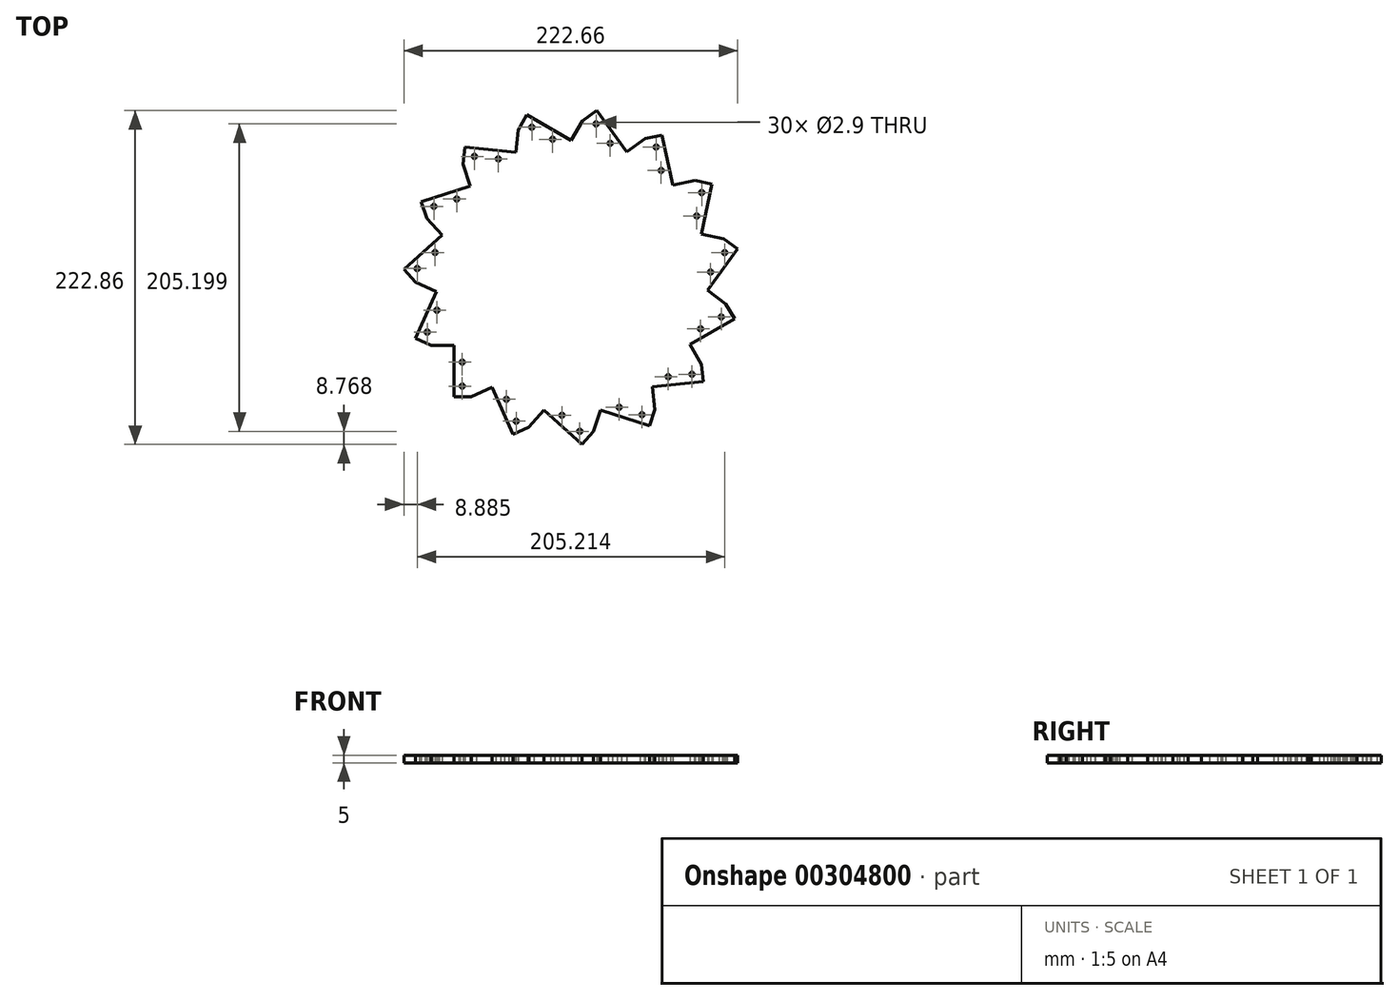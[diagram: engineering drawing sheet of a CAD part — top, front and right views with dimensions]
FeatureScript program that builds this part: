
annotation { "Feature Type Name" : "Feature", "Feature Type Description" : "" }
export const myFeature = defineFeature(function(context is Context, id is Id, definition is map)
    precondition{}
    {
        {
            var Q0;
            Q0=qCreatedBy(makeId("Top.planeOp"),FACE);
            var sketch = newSketch(context, id + "F0", { "sketchPlane" : qUnion([Q0])});
            skCircle(sketch, "E0.1.0", {"center": v(-64.96, 80.33) * mm, "radius": 1.45 * mm});
            skCircle(sketch, "E0.1.1", {"center": v(-49.05, 78.66) * mm, "radius": 1.45 * mm});
            skCircle(sketch, "E0.2.0", {"center": v(-92.02, 46.97) * mm, "radius": 1.45 * mm});
            skCircle(sketch, "E0.2.1", {"center": v(-76.8, 51.91) * mm, "radius": 1.45 * mm});
            skCircle(sketch, "E0.3.0", {"center": v(-103.16, 5.48) * mm, "radius": 1.45 * mm});
            skCircle(sketch, "E0.3.1", {"center": v(-91.27, 16.19) * mm, "radius": 1.45 * mm});
            skCircle(sketch, "E0.4.0", {"center": v(-96.47, -36.96) * mm, "radius": 1.45 * mm});
            skCircle(sketch, "E0.4.1", {"center": v(-89.97, -22.34) * mm, "radius": 1.45 * mm});
            skCircle(sketch, "E0.5.0", {"center": v(-73.1, -73) * mm, "radius": 1.45 * mm});
            skCircle(sketch, "E0.5.1", {"center": v(-73.1, -57) * mm, "radius": 1.45 * mm});
            skCircle(sketch, "E0.6.0", {"center": v(-37.1, -96.42) * mm, "radius": 1.45 * mm});
            skCircle(sketch, "E0.6.1", {"center": v(-43.6, -81.8) * mm, "radius": 1.45 * mm});
            skCircle(sketch, "E0.7.0", {"center": v(5.33, -103.17) * mm, "radius": 1.45 * mm});
            skCircle(sketch, "E0.7.1", {"center": v(-6.56, -92.47) * mm, "radius": 1.45 * mm});
            skCircle(sketch, "E0.8.0", {"center": v(46.84, -92.08) * mm, "radius": 1.45 * mm});
            skCircle(sketch, "E0.8.1", {"center": v(31.62, -87.14) * mm, "radius": 1.45 * mm});
            skCircle(sketch, "E0.9.0", {"center": v(80.24, -65.07) * mm, "radius": 1.45 * mm});
            skCircle(sketch, "E0.9.1", {"center": v(64.33, -66.74) * mm, "radius": 1.45 * mm});
            skCircle(sketch, "E0.10.0", {"center": v(99.77, -26.8) * mm, "radius": 1.45 * mm});
            skCircle(sketch, "E0.10.1", {"center": v(85.91, -34.8) * mm, "radius": 1.45 * mm});
            skCircle(sketch, "E0.11.0", {"center": v(102.05, 16.09) * mm, "radius": 1.45 * mm});
            skCircle(sketch, "E0.11.1", {"center": v(92.64, 3.15) * mm, "radius": 1.45 * mm});
            skCircle(sketch, "E0.12.0", {"center": v(86.68, 56.2) * mm, "radius": 1.45 * mm});
            skCircle(sketch, "E0.12.1", {"center": v(83.36, 40.56) * mm, "radius": 1.45 * mm});
            skCircle(sketch, "E0.13.0", {"center": v(56.33, 86.6) * mm, "radius": 1.45 * mm});
            skCircle(sketch, "E0.13.1", {"center": v(59.65, 70.95) * mm, "radius": 1.45 * mm});
            skCircle(sketch, "E0.14.0", {"center": v(16.23, 102.03) * mm, "radius": 1.45 * mm});
            skCircle(sketch, "E0.14.1", {"center": v(25.64, 89.08) * mm, "radius": 1.45 * mm});
            skPoint(sketch, "E0.center", {"position": v(0, 0) * mm});
            skLineSegment(sketch, "E1", {"start": v(-29.98, 108.07) * mm, "end": v(-0.35, 90.97) * mm});
            skLineSegment(sketch, "E2", {"start": v(-29.98, 108.07) * mm, "end": v(-35.73, 98.11) * mm});
            skLineSegment(sketch, "E3", {"start": v(-35.73, 98.11) * mm, "end": v(-37.32, 82.96) * mm});
            skLineSegment(sketch, "E4.1.0", {"start": v(-72.55, 75.1) * mm, "end": v(-67.84, 60.6) * mm});
            skLineSegment(sketch, "E4.1.1", {"start": v(-71.35, 86.53) * mm, "end": v(-72.55, 75.1) * mm});
            skLineSegment(sketch, "E4.1.2", {"start": v(-71.35, 86.53) * mm, "end": v(-37.32, 82.96) * mm});
            skLineSegment(sketch, "E4.2.0", {"start": v(-96.82, 39.1) * mm, "end": v(-86.62, 27.77) * mm});
            skLineSegment(sketch, "E4.2.1", {"start": v(-100.37, 50.03) * mm, "end": v(-96.82, 39.1) * mm});
            skLineSegment(sketch, "E4.2.2", {"start": v(-100.37, 50.03) * mm, "end": v(-67.84, 60.6) * mm});
            skLineSegment(sketch, "E4.3.0", {"start": v(-104.35, -3.66) * mm, "end": v(-90.43, -9.86) * mm});
            skLineSegment(sketch, "E4.3.1", {"start": v(-112.05, 4.88) * mm, "end": v(-104.35, -3.66) * mm});
            skLineSegment(sketch, "E4.3.2", {"start": v(-112.05, 4.88) * mm, "end": v(-86.62, 27.77) * mm});
            skLineSegment(sketch, "E4.4.0", {"start": v(-93.84, -45.8) * mm, "end": v(-78.6, -45.8) * mm});
            skLineSegment(sketch, "E4.4.1", {"start": v(-104.35, -41.11) * mm, "end": v(-93.84, -45.8) * mm});
            skLineSegment(sketch, "E4.4.2", {"start": v(-104.35, -41.11) * mm, "end": v(-90.43, -9.86) * mm});
            skLineSegment(sketch, "E4.5.0", {"start": v(-67.1, -80) * mm, "end": v(-53.18, -73.8) * mm});
            skLineSegment(sketch, "E4.5.1", {"start": v(-78.6, -80) * mm, "end": v(-67.1, -80) * mm});
            skLineSegment(sketch, "E4.5.2", {"start": v(-78.6, -80) * mm, "end": v(-78.6, -45.8) * mm});
            skLineSegment(sketch, "E4.6.0", {"start": v(-28.76, -100.38) * mm, "end": v(-18.57, -89.05) * mm});
            skLineSegment(sketch, "E4.6.1", {"start": v(-39.27, -105.05) * mm, "end": v(-28.76, -100.38) * mm});
            skLineSegment(sketch, "E4.6.2", {"start": v(-39.27, -105.05) * mm, "end": v(-53.18, -73.8) * mm});
            skLineSegment(sketch, "E4.7.0", {"start": v(14.55, -103.4) * mm, "end": v(19.26, -88.9) * mm});
            skLineSegment(sketch, "E4.7.1", {"start": v(6.86, -111.94) * mm, "end": v(14.55, -103.4) * mm});
            skLineSegment(sketch, "E4.7.2", {"start": v(6.86, -111.94) * mm, "end": v(-18.57, -89.05) * mm});
            skLineSegment(sketch, "E4.8.0", {"start": v(55.35, -88.54) * mm, "end": v(53.76, -73.39) * mm});
            skLineSegment(sketch, "E4.8.1", {"start": v(51.8, -99.48) * mm, "end": v(55.35, -88.54) * mm});
            skLineSegment(sketch, "E4.8.2", {"start": v(51.8, -99.48) * mm, "end": v(19.26, -88.9) * mm});
            skLineSegment(sketch, "E4.9.0", {"start": v(86.58, -58.37) * mm, "end": v(78.96, -45.18) * mm});
            skLineSegment(sketch, "E4.9.1", {"start": v(87.78, -69.8) * mm, "end": v(86.58, -58.37) * mm});
            skLineSegment(sketch, "E4.9.2", {"start": v(87.78, -69.8) * mm, "end": v(53.76, -73.39) * mm});
            skLineSegment(sketch, "E4.10.0", {"start": v(102.83, -18.11) * mm, "end": v(90.5, -9.16) * mm});
            skLineSegment(sketch, "E4.10.1", {"start": v(108.58, -28.07) * mm, "end": v(102.83, -18.11) * mm});
            skLineSegment(sketch, "E4.10.2", {"start": v(108.58, -28.07) * mm, "end": v(78.96, -45.18) * mm});
            skLineSegment(sketch, "E4.11.0", {"start": v(101.3, 25.28) * mm, "end": v(86.4, 28.45) * mm});
            skLineSegment(sketch, "E4.11.1", {"start": v(110.61, 18.52) * mm, "end": v(101.3, 25.28) * mm});
            skLineSegment(sketch, "E4.11.2", {"start": v(110.61, 18.52) * mm, "end": v(90.5, -9.16) * mm});
            skLineSegment(sketch, "E4.12.0", {"start": v(82.27, 64.3) * mm, "end": v(67.36, 61.13) * mm});
            skLineSegment(sketch, "E4.12.1", {"start": v(93.52, 61.9) * mm, "end": v(82.27, 64.3) * mm});
            skLineSegment(sketch, "E4.12.2", {"start": v(93.52, 61.9) * mm, "end": v(86.4, 28.45) * mm});
            skLineSegment(sketch, "E4.13.0", {"start": v(49, 92.2) * mm, "end": v(36.68, 83.25) * mm});
            skLineSegment(sketch, "E4.13.1", {"start": v(60.25, 94.6) * mm, "end": v(49, 92.2) * mm});
            skLineSegment(sketch, "E4.13.2", {"start": v(60.25, 94.6) * mm, "end": v(67.36, 61.13) * mm});
            skLineSegment(sketch, "E4.14.0", {"start": v(7.26, 104.16) * mm, "end": v(-0.35, 90.97) * mm});
            skLineSegment(sketch, "E4.14.1", {"start": v(16.57, 110.92) * mm, "end": v(7.26, 104.16) * mm});
            skLineSegment(sketch, "E4.14.2", {"start": v(16.57, 110.92) * mm, "end": v(36.68, 83.25) * mm});
            skCircle(sketch, "E5", {"center": v(-26.67, 99.8) * mm, "radius": 1.45 * mm});
            skCircle(sketch, "E6", {"center": v(-12.81, 91.8) * mm, "radius": 1.45 * mm});
            skSolve(sketch);
        }
        {
            var Q0;
            Q0 = qSketchRegion(id + "F0", true);
            extrude(context, id + "F1", {"entities" : qUnion([Q0]), "depth" : 5 * mm});
        }
    });
